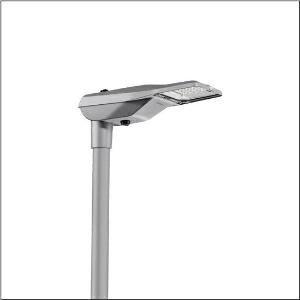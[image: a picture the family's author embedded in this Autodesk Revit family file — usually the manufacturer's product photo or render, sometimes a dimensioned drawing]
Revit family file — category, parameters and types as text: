
# Revit family: streetlight_sl_21_iq_micro___stw1_0a_5xe1e31y08db_aea3
name_source: partatom
category: Lighting Fixtures
units: mm (PartAtom-declared; Revit-internal decimal feet)

## family parameters
Cut with Voids When Loaded = No
Host = Face
Light Source = No
Part Type = Normal
Room Calculation Point = No
Round Connector Dimension = Use Diameter
Shared = No

## types (1)
- --- (1 x LED, 5110 lm, 39.1 W, 3000K)
    Apparent Load = 39 VA
    CIE Flux Codes = 38 75 98 100 100
    Color Rendering = 70
    Color Temperature = 3000K
    Default Elevation = 1800 mm
    Description = Streetlight SL 21 iQ micro, mast luminaire, primary light control with lens, of PMMA, primary optical cover: cover, of toughened safety glass, transparent, light distribution: STW1.0a, light emission: direct distribution, primary light characteristic: asymmetric, installation type: post-top, side-entry, LED, High Power LED, rated luminous flux: 5.110lm, luminous efficacy: 131lm/W, light colour: 730, colour temperature: 3000K, control: presetting dimming logarithmic, Street-Remote, Auto-Match, Temp-Guard, Lumen-Switch, Night-Set, Smart-Wire, Light-Fading, Desk-Remote (wireless, voltage-free reading and setting of iQ features in the workshop via application-optimized NFC function/RFID function), optimised constant luminous flux control (CLO 2.0), mains connection: 220..240V, AC, 50/60Hz, start of lifetime: 39W, end of service life: 41W, reduction: 17W, luminaire housing, of diecast aluminium, powder-coated, Siteco® metallic grey (DB 702S), corrosivity category C5 mid according to DIN EN ISO 12944, please order mast flange separately, inclination adjustable: 0°, 5°, 10°, 15°, sealing non-destructively replaceable, multi-level sealing system, length: 528mm, width: 235mm, height: 110mm, mast flange for spigot size: 42mm (side-entry): 5XC10008XM4, 60/48mm (side-entry/post-top): 5XC10108XM2, 76/60mm (side-entry/post-top): 5XC10108XM1, Smart Interface below and above, protection rating (complete): IP66, insulation class (complete): insulation class II (safety insulation), certification: CE, ENEC, ENEC+, VDE, impact resistance: IK09, permissible operating ambient temperature for outdoor applications: -40..+50°C, standard-compliant lighting for roads and squares, packaging unit: 1 piece

Light Distribution: STW1.0a
    Height = 110 mm
    Lamp = 1 x LED
    Lamp Light Flux = 5110 lm
    Lamp Power = 39.1 W
    Lamp count = 1
    Length = 528 mm
    Luminous efficacy = 131 lm/W
    Manufacturer = Siteco
    ModVariant = No
    Model = 5XE1E31Y08DB
    Number of Poles = 1
    OnlyDefault = Yes
    Power Factor = 1
    Product Name = Streetlight SL 21 iQ micro | STW1.0a
    Product group = mast luminaire | pylon top
    ProductGroupID = 6100
    Protection Class = Protection class II
    Protection Degree = IP 66
    RLX_Detail_Level = 1
    RLX_Emergency_Light_Flux = 0 lm
    RLX_Emergency_Type = 0
    RLX_Emergency_Type_DB = No
    RlxData = <blob elided: 98781 chars, md5=ae1fff33>
    Socket = socket
    Standby Power = 0 W
    System Light Flux = 5110 lm
    System Power = 39 W
    Type Comments = factory setting: luminous flux: 100 % | dim-lin: 254 | 765 mA
    Type Image = l_1007239.jpg
    URL = http://relux.com
    VarID = @adj_044417
    Voltage = 0 V
    Weight = 0.00 kg
    Width = 235 mm

## geometry (parser evidence)
native form markers: Blend x4, Sweep x10
no freeform markers — native parametric forms only
